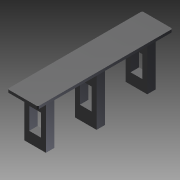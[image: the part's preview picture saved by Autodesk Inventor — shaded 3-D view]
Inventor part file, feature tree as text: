
AUTODESK INVENTOR PART (.ipt)
format: ipt  version: 2015 (Build 190159000, 159)  size: 121,856 bytes
history: native  units: in
note: dims shown in document units (in); Inventor stores cm internally (conversion verified against a paired STEP export)
features: other x7, extrude x4, sketch x4
ambient origin geometry x8: Origin, YZ Plane, XZ Plane, XY Plane, X Axis, Y Axis, Z Axis, Center Point
bodies: Solid1 (feature_tree)
feature tree (15):
  extrude  "Extrusion1"  Depth=0.031in TaperAngle=0.0deg
  extrude  "Extrusion2"  Depth=0.031in TaperAngle=0.0deg
  extrude  "Extrusion3"  [1 undecoded]
  extrude  "Extrusion4"  [1 undecoded]
  other  "to_body_XY"
  other  "to_body_YZ"
  other  "to_body_ZX"
  other  "to_body_X"
  other  "to_body_Y"
  other  "to_body_Z"
  other  "to_body_Center"
  sketch  "Sketch_1"  dims[d0=0.01in d1=0.0in d2=0.031in d3=0.0in]
  sketch  "Sketch_2"  dims[d4=0.031in d5=0.0in d6=0.031in d7=0.0in]
  sketch  "Sketch_3"
  sketch  "Sketch_4"
note: 2 required parameter values undecoded (feature->parameter linkage not recoverable at this tier; creation-order binding heuristic only, values carry confidence <= 0.55)
